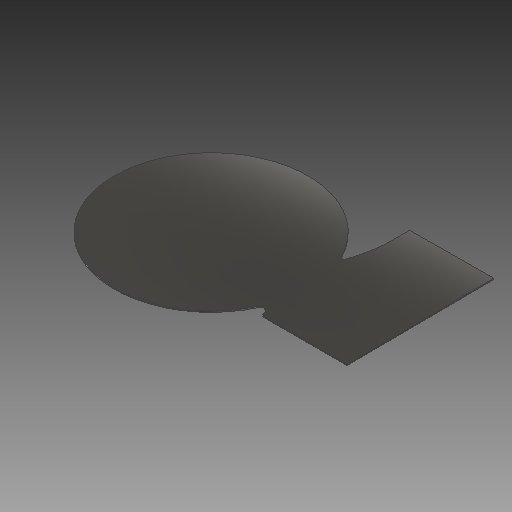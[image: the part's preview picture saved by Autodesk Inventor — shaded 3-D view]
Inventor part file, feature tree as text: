
AUTODESK INVENTOR PART (.ipt)
format: ipt  version: 2018 (Build 220112000, 112)  size: 112,640 bytes
history: native  units: mm
features: other x3, sketch x1
ambient origin geometry x8: Origin, YZ Plane, XZ Plane, XY Plane, X Axis, Y Axis, Z Axis, Center Point
bodies: Volumenkörper1 (feature_tree)
feature tree (4):
  other  "Solarpanel.ipt"
  other  "Volumenkörper1::Solarpanel.ipt"
  other  "Bezeichnung1"
  sketch  "Skizze6"  dims[d0=10.0mm]
